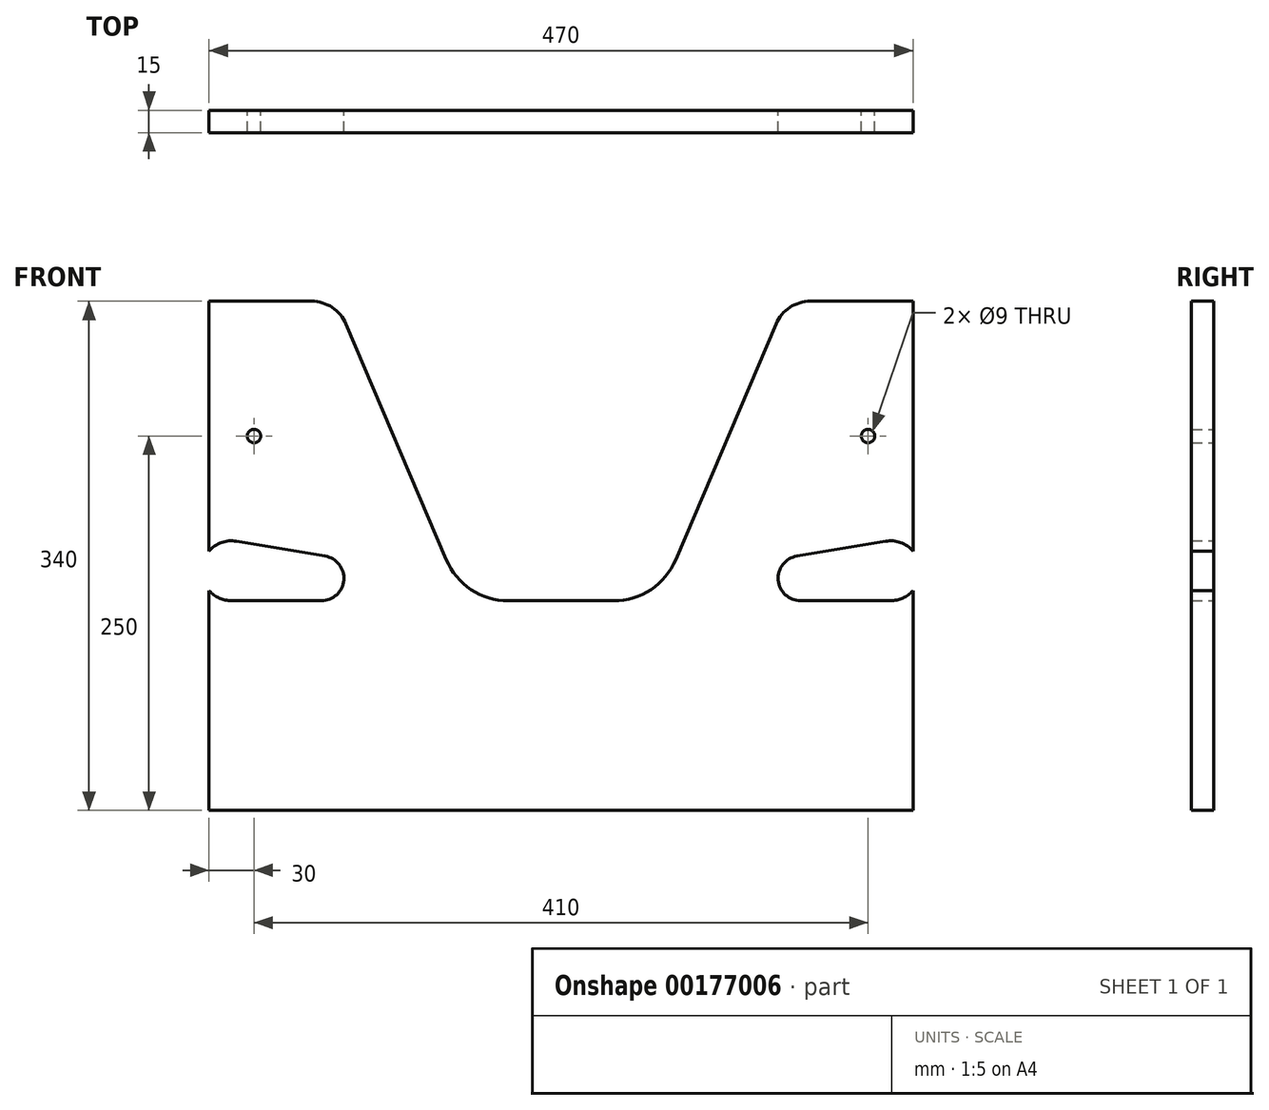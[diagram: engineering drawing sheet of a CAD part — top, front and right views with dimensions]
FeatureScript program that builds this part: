
annotation { "Feature Type Name" : "Feature", "Feature Type Description" : "" }
export const myFeature = defineFeature(function(context is Context, id is Id, definition is map)
    precondition{}
    {
        {
            var Q0;
            Q0=qCreatedBy(makeId("Front.planeOp"),FACE);
            var sketch = newSketch(context, id + "F0", { "sketchPlane" : qUnion([Q0])});
            skLineSegment(sketch, "E0.bottom", {"start": v(-235, 170) * mm, "end": v(-166.54, 170) * mm});
            skLineSegment(sketch, "E0.top", {"start": v(-235, -170) * mm, "end": v(0, -170) * mm});
            skLineSegment(sketch, "E0.left", {"start": v(-235, 170) * mm, "end": v(-235, 3.23) * mm});
            skLineSegment(sketch, "E0.right", {"start": v(0, 170) * mm, "end": v(0, -170) * mm, "construction": true});
            skLineSegment(sketch, "E1", {"start": v(-220, -30) * mm, "end": v(-160, -30) * mm});
            skLineSegment(sketch, "E2", {"start": v(-143.53, 154.78) * mm, "end": v(-76.64, -2.6) * mm});
            skArc(sketch, "E3", {"start": v(-76.64, -2.6) * mm, "mid": v(-60.06, -22.53) * mm, "end": v(-35.23, -30) * mm});
            skArc(sketch, "E4", {"start": v(-143.53, 154.78) * mm, "mid": v(-152.75, 165.85) * mm, "end": v(-166.54, 170) * mm});
            skCircle(sketch, "E5", {"center": v(-205, 80) * mm, "radius": 4.5 * mm});
            skArc(sketch, "E6", {"start": v(-216.69, 9.72) * mm, "mid": v(-226.69, 8.85) * mm, "end": v(-235, 3.23) * mm});
            skArc(sketch, "E7", {"start": v(-160, -30) * mm, "mid": v(-145.05, -16.25) * mm, "end": v(-157.52, -0.2) * mm});
            skLineSegment(sketch, "E8", {"start": v(-216.69, 9.72) * mm, "end": v(-157.52, -0.2) * mm});
            skLineSegment(sketch, "E9.trimOffspring", {"start": v(-35.23, -30) * mm, "end": v(0, -30) * mm});
            skPoint(sketch, "E10.orphan", {"position": v(-65, -30) * mm});
            skArc(sketch, "E11.trimOffspring", {"start": v(-235, -23.23) * mm, "mid": v(-228.23, -28.23) * mm, "end": v(-220, -30) * mm});
            skLineSegment(sketch, "E12.trimOffspring", {"start": v(-235, -23.23) * mm, "end": v(-235, -170) * mm});
            skPoint(sketch, "E13.orphan", {"position": v(-235, -30) * mm});
            skPoint(sketch, "E14.orphan", {"position": v(-150, 170) * mm});
            skLineSegment(sketch, "E15.MirrorCS", {"start": v(235, -170) * mm, "end": v(0, -170) * mm});
            skLineSegment(sketch, "E16.MirrorCS", {"start": v(235, -23.23) * mm, "end": v(235, -170) * mm});
            skArc(sketch, "E17.MirrorCS", {"start": v(235, -23.23) * mm, "mid": v(228.23, -28.23) * mm, "end": v(220, -30) * mm});
            skLineSegment(sketch, "E18.MirrorCS", {"start": v(220, -30) * mm, "end": v(160, -30) * mm});
            skArc(sketch, "E19.MirrorCS", {"start": v(160, -30) * mm, "mid": v(145.05, -16.25) * mm, "end": v(157.52, -0.2) * mm});
            skLineSegment(sketch, "E20.MirrorCS", {"start": v(216.69, 9.72) * mm, "end": v(157.52, -0.2) * mm});
            skArc(sketch, "E21.MirrorCS", {"start": v(216.69, 9.72) * mm, "mid": v(226.69, 8.85) * mm, "end": v(235, 3.23) * mm});
            skLineSegment(sketch, "E22.MirrorCS", {"start": v(235, 170) * mm, "end": v(235, 3.23) * mm});
            skLineSegment(sketch, "E23.MirrorCS", {"start": v(235, 170) * mm, "end": v(166.54, 170) * mm});
            skArc(sketch, "E24.MirrorCS", {"start": v(143.53, 154.78) * mm, "mid": v(152.75, 165.85) * mm, "end": v(166.54, 170) * mm});
            skLineSegment(sketch, "E25.MirrorCS", {"start": v(143.53, 154.78) * mm, "end": v(76.64, -2.6) * mm});
            skArc(sketch, "E26.MirrorCS", {"start": v(76.64, -2.6) * mm, "mid": v(60.06, -22.53) * mm, "end": v(35.23, -30) * mm});
            skLineSegment(sketch, "E27.MirrorCS", {"start": v(35.23, -30) * mm, "end": v(0, -30) * mm});
            skCircle(sketch, "E28.MirrorC", {"center": v(205, 80) * mm, "radius": 4.5 * mm});
            skSolve(sketch);
        }
        {
            var Q0;
            Q0=makeQuery(id+"F0.imprint","IMPRINT",FACE,{"disambiguationData":[TD([[makeQuery(id+"F0.imprint","IMPRINT",EDGE,{"derivedFrom":sQuery(id+"F0.wireOp",EDGE,"E0.bottom")}),-1.0]])]});
            extrude(context, id + "F1", {"entities" : qUnion([Q0]), "depth" : 15 * mm});
        }
    });
